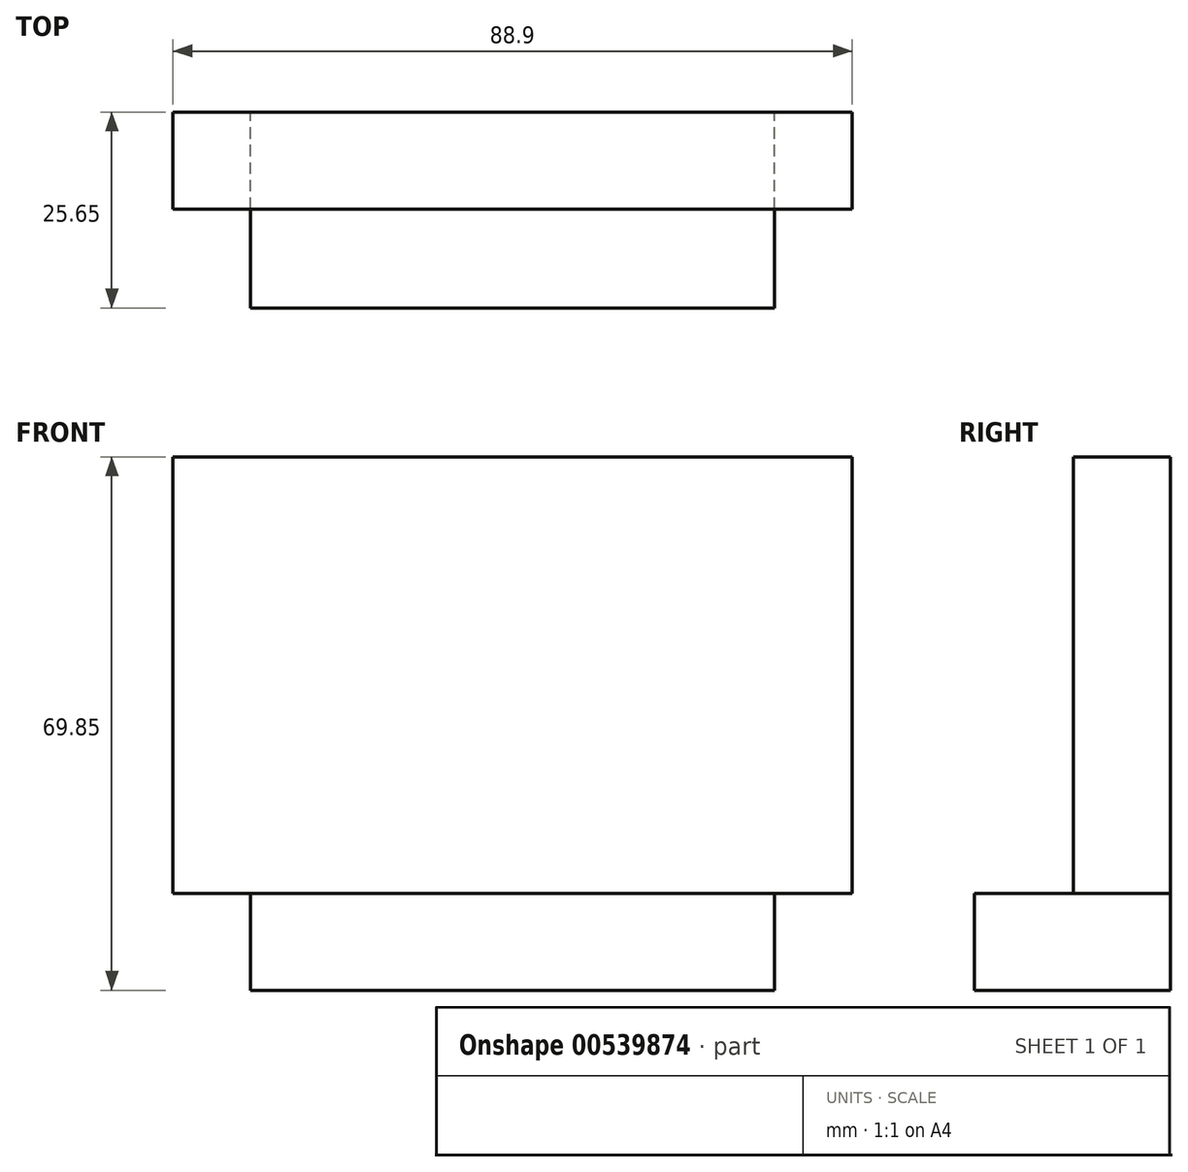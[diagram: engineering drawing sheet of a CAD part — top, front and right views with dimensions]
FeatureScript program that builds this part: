
annotation { "Feature Type Name" : "Feature", "Feature Type Description" : "" }
export const myFeature = defineFeature(function(context is Context, id is Id, definition is map)
    precondition{}
    {
        {
            var Q0;
            Q0=qCreatedBy(makeId("Front.planeOp"),FACE);
            var sketch = newSketch(context, id + "F0", { "sketchPlane" : qUnion([Q0])});
            skLineSegment(sketch, "E0", {"start": v(0, 0) * mm, "end": v(-44.45, 0) * mm});
            skLineSegment(sketch, "E1", {"start": v(0, 0) * mm, "end": v(44.45, 0) * mm});
            skLineSegment(sketch, "E2", {"start": v(-44.45, 0) * mm, "end": v(-44.45, 57.15) * mm});
            skLineSegment(sketch, "E3", {"start": v(-44.45, 57.15) * mm, "end": v(44.45, 57.15) * mm});
            skLineSegment(sketch, "E4", {"start": v(44.45, 0) * mm, "end": v(44.45, 57.15) * mm});
            skLineSegment(sketch, "E5", {"start": v(0, 0) * mm, "end": v(34.3, 0) * mm});
            skLineSegment(sketch, "E6", {"start": v(0, 0) * mm, "end": v(-34.3, 0) * mm});
            skLineSegment(sketch, "E7", {"start": v(-34.3, 0) * mm, "end": v(-34.3, -53.34) * mm});
            skLineSegment(sketch, "E8", {"start": v(34.3, 0) * mm, "end": v(34.3, -53.34) * mm});
            skLineSegment(sketch, "E9", {"start": v(-34.3, -53.34) * mm, "end": v(-34.3, -66.04) * mm});
            skLineSegment(sketch, "E10", {"start": v(34.3, -53.34) * mm, "end": v(34.3, -66.04) * mm});
            skLineSegment(sketch, "E11", {"start": v(-34.3, -66.04) * mm, "end": v(34.3, -66.04) * mm});
            skSolve(sketch);
        }
        {
            var Q0;
            Q0=makeQuery(id+"F0.imprint","IMPRINT",FACE,{"disambiguationData":[TD([[makeQuery(id+"F0.imprint","IMPRINT",EDGE,{"derivedFrom":sQuery(id+"F0.wireOp",EDGE,"E5")}),-1.0]])]});
            var Q1;
            Q1=makeQuery(id+"F0.imprint","IMPRINT",FACE,{"disambiguationData":[TD([[makeQuery(id+"F0.imprint","IMPRINT",EDGE,{"derivedFrom":sQuery(id+"F0.wireOp",EDGE,"E0")}),-1.0]])]});
            extrude(context, id + "F1", {"entities" : qUnion([Q0, Q1]), "depth" : 12.7 * mm, "offsetDistance" : 25.4 * mm});
        }
        {
            var Q0;
            Q0=qCreatedBy(makeId("Front.planeOp"),FACE);
            var sketch = newSketch(context, id + "F2", { "sketchPlane" : qUnion([Q0])});
            skPoint(sketch, "E12.start.orphan", {"position": v(-61.24, 0) * mm});
            skPoint(sketch, "E13.start.orphan", {"position": v(34.3, 0) * mm});
            skLineSegment(sketch, "E14", {"start": v(-34.3, 0) * mm, "end": v(34.3, 0) * mm});
            skLineSegment(sketch, "E15", {"start": v(-34.3, 0) * mm, "end": v(-34.3, -12.7) * mm});
            skLineSegment(sketch, "E16", {"start": v(34.3, 0) * mm, "end": v(34.3, -12.7) * mm});
            skLineSegment(sketch, "E17", {"start": v(-34.3, -12.7) * mm, "end": v(34.3, -12.7) * mm});
            skSolve(sketch);
        }
        {
            var Q0;
            Q0 = qSketchRegion(id + "F2", true);
            extrude(context, id + "F3", {"entities" : qUnion([Q0]), "operationType" : NewBodyOperationType.ADD, "depth" : 25.65 * mm, "offsetDistance" : 25.4 * mm});
        }
    });
